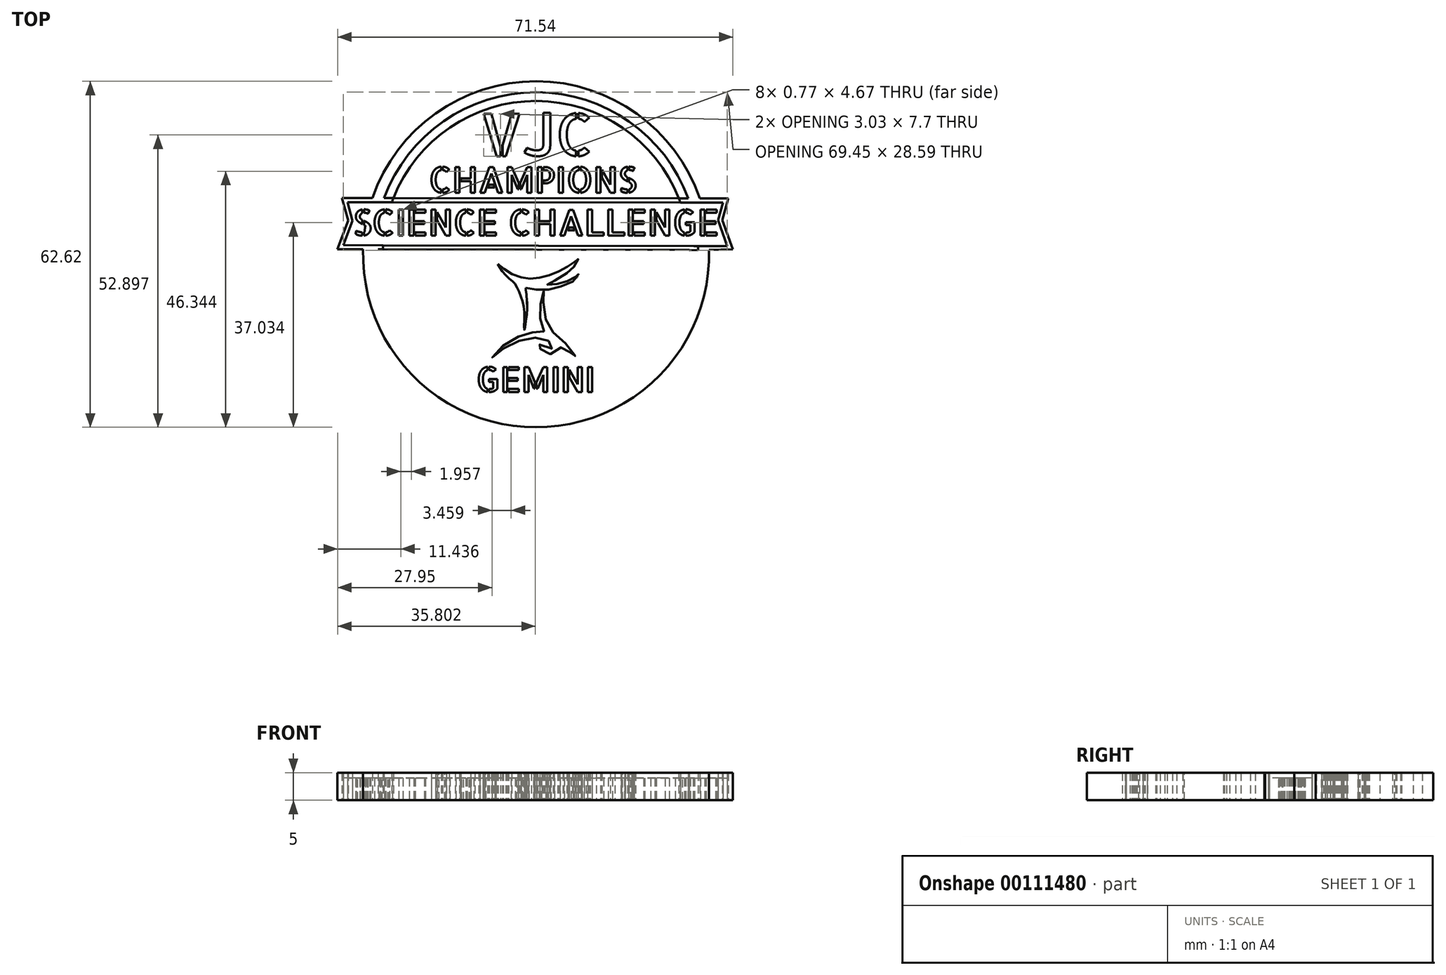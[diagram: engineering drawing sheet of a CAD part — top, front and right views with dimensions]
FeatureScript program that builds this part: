
annotation { "Feature Type Name" : "Feature", "Feature Type Description" : "" }
export const myFeature = defineFeature(function(context is Context, id is Id, definition is map)
    precondition{}
    {
        {
            var Q0;
            Q0=qCreatedBy(makeId("Top.planeOp"),FACE);
            var sketch = newSketch(context, id + "F0", { "sketchPlane" : qUnion([Q0])});
            skCircle(sketch, "E0", {"center": v(0.94, -3) * mm, "radius": 27.74 * mm});
            skPoint(sketch, "E0.first.point", {"position": v(1.58, 24.74) * mm});
            skPoint(sketch, "E0.second.point", {"position": v(0.52, -30.73) * mm});
            skPoint(sketch, "E0.third.point", {"position": v(-26.76, -1.33) * mm});
            skText(sketch, "E1", { "text": "CHAMPIONS", "fontName": "AllertaStencil-Regular.ttf"});
            skText(sketch, "E2", { "text": "GEMINI", "fontName": "AllertaStencil-Regular.ttf"});
            skLineSegment(sketch, "E3", {"start": v(-24.87, 7.2) * mm, "end": v(-34.2, 7.2) * mm});
            skLineSegment(sketch, "E4", {"start": v(-34.2, 7.2) * mm, "end": v(-33.08, 3.11) * mm});
            skLineSegment(sketch, "E5", {"start": v(-33.08, 3.11) * mm, "end": v(-35, -2.1) * mm});
            skLineSegment(sketch, "E6", {"start": v(-35, -2.1) * mm, "end": v(-26.8, -2.1) * mm});
            skLineSegment(sketch, "E7", {"start": v(26.78, 7.1) * mm, "end": v(35.71, 7.1) * mm});
            skLineSegment(sketch, "E8", {"start": v(35.71, 7.1) * mm, "end": v(34.66, 3.21) * mm});
            skLineSegment(sketch, "E9", {"start": v(34.66, 3.21) * mm, "end": v(36.55, -2.1) * mm});
            skLineSegment(sketch, "E10", {"start": v(36.55, -2.1) * mm, "end": v(28.67, -2.25) * mm});
            skFitSpline(sketch, "E11", {"points": [v(-6, -4.72) * mm, v(-5.23, -5.35) * mm, v(-3.9, -6.35) * mm, v(-2.48, -6.98) * mm, v(-0.85, -7.35) * mm, v(0.35, -7.37) * mm, v(2.08, -7.15) * mm, v(3.86, -6.6) * mm, v(5.5, -5.84) * mm, v(6.83, -5.05) * mm, v(7.95, -4.34) * mm, v(8.2, -4.17) * mm, v(8.54, -3.89) * mm, v(8.14, -4.78) * mm, v(7.2, -5.82) * mm, v(5.2, -7.28) * mm, v(2.9, -8.45) * mm, v(3.98, -8.47) * mm, v(5.87, -8.12) * mm, v(7.76, -7.26) * mm, v(8.43, -6.75) * mm, v(8.6, -6.46) * mm, v(8.47, -7.15) * mm, v(6.46, -8.4) * mm, v(3.8, -9.28) * mm, v(1.11, -9.42) * mm, v(-0.95, -9.06) * mm], "startDerivative": vector(22.31, -18.25) * mm, "endDerivative": vector(-43, 9.84) * mm});
            skFitSpline(sketch, "E12", {"points": [v(-6, -4.72) * mm, v(-5.19, -6.01) * mm, v(-3.81, -7.48) * mm, v(-3.02, -8.2) * mm, v(-2.26, -9.47) * mm, v(-1.53, -11.45) * mm, v(-1.17, -13.95) * mm, v(-1.2, -16.67) * mm, v(-0.95, -15.45) * mm, v(-0.68, -11.98) * mm, v(-0.91, -9.36) * mm, v(-0.95, -9.06) * mm], "startDerivative": vector(8.3, -15) * mm, "endDerivative": vector(-0.86, 6) * mm});
            skFitSpline(sketch, "E13", {"points": [v(2.34, -9.66) * mm, v(2.02, -10.62) * mm, v(1.67, -12.76) * mm, v(1.67, -14.3) * mm, v(2.06, -16.19) * mm, v(2.36, -16.95) * mm, v(1.82, -16.92) * mm, v(-0.01, -17.17) * mm, v(-1.66, -17.64) * mm, v(-3.97, -18.79) * mm, v(-6.02, -20.44) * mm, v(-6.96, -21.68) * mm, v(-5.91, -20.77) * mm, v(-3.67, -19.33) * mm, v(-1.3, -18.4) * mm, v(0.83, -18.07) * mm, v(2.42, -18.3) * mm, v(3.7, -19.03) * mm, v(4.04, -19.68) * mm, v(3.45, -20.21) * mm, v(1.98, -19.81) * mm, v(1.3, -18.87) * mm, v(1.45, -19.8) * mm, v(2.36, -20.56) * mm, v(3.3, -21.02) * mm, v(4.84, -20.7) * mm, v(5.53, -19.8) * mm, v(6.38, -20.28) * mm, v(7.16, -20.84) * mm, v(8.14, -21.87) * mm, v(7.64, -20.68) * mm, v(6.28, -19.14) * mm, v(4.5, -17.53) * mm, v(3.33, -16.29) * mm, v(2.56, -14.18) * mm, v(2.24, -11.68) * mm, v(2.33, -10.24) * mm, v(2.34, -9.66) * mm]});
            skLineSegment(sketch, "E14", {"start": v(-24.87, 7.2) * mm, "end": v(28.1, 7.1) * mm});
            skLineSegment(sketch, "E15", {"start": v(-27.68, -2.1) * mm, "end": v(29.48, -2.24) * mm});
            skText(sketch, "E16", { "text": "SCIENCE CHALLENGE", "fontName": "AllertaStencil-Regular.ttf"});
            skText(sketch, "E17", { "text": "VJC", "fontName": "AllertaStencil-Regular.ttf"});
            skCircle(sketch, "E18.0", {"center": v(0.94, -3) * mm, "radius": 29.33 * mm});
            skCircle(sketch, "E19.0", {"center": v(0.94, -3) * mm, "radius": 31.31 * mm});
            skLineSegment(sketch, "E20.0", {"start": v(-24.87, 6.45) * mm, "end": v(28.1, 6.35) * mm});
            skLineSegment(sketch, "E21.0", {"start": v(-24.87, 6.45) * mm, "end": v(-33.21, 6.45) * mm});
            skLineSegment(sketch, "E22", {"start": v(28.1, 6.35) * mm, "end": v(34.73, 6.35) * mm});
            skLineSegment(sketch, "E23.0", {"start": v(-27.68, -1.35) * mm, "end": v(29.48, -1.49) * mm});
            skLineSegment(sketch, "E24", {"start": v(-27.68, -1.35) * mm, "end": v(-33.91, -1.33) * mm});
            skLineSegment(sketch, "E25", {"start": v(29.48, -1.49) * mm, "end": v(35.54, -1.5) * mm});
            skLineSegment(sketch, "E26.0", {"start": v(34.73, 6.35) * mm, "end": v(33.88, 3.18) * mm});
            skLineSegment(sketch, "E27.0", {"start": v(33.88, 3.18) * mm, "end": v(35.54, -1.5) * mm});
            skLineSegment(sketch, "E28.0", {"start": v(-32.3, 3.08) * mm, "end": v(-33.91, -1.33) * mm});
            skLineSegment(sketch, "E29.trimOffspring", {"start": v(-33.21, 6.45) * mm, "end": v(-32.3, 3.08) * mm});
            const initialGuessF0  = {"E1": [-0.01849, 0.00816, 1, 0, 0.00464], "E2": [-0.00992, -0.0279, 1, 0, 0.0045], "E16": [-0.03222, 0.0004, 1, 0, 0.00467], "E17": [-0.00918, 0.01479, 1, 0, 0.00766]};
            skSetInitialGuess(sketch, initialGuessF0);
            skSolve(sketch);
        }
        {
            var Q0;
            Q0=makeQuery(id+"F0.imprint","IMPRINT",FACE,{"disambiguationData":[TD([[makeQuery(id+"F0.imprint","IMPRINT",EDGE,{"derivedFrom":sQuery(id+"F0.wireOp",EDGE,"E1.sketch_text.stroke-0")}),1.0]])]});
            var Q1;
            {var subQ0=sQuery(id+"F0.wireOp",EDGE,"E19.0");var subQ1=sQuery(id+"F0.wireOp",EDGE,"E3");var subQ2=makeQuery(id+"F0.imprint","INTERSECT",VERTEX,{"derivedFrom":[subQ1,subQ0]});Q1=makeQuery(id+"F0.imprint","IMPRINT",FACE,{"disambiguationData":[TD([[makeQuery(id+"F0.imprint","IMPRINT",EDGE,{"disambiguationData":[TD([[subQ2,1.0]])],"derivedFrom":subQ1}),-1.0]])]});}
            var Q2;
            Q2=makeQuery(id+"F0.imprint","IMPRINT",FACE,{"disambiguationData":[TD([[makeQuery(id+"F0.imprint","IMPRINT",EDGE,{"derivedFrom":sQuery(id+"F0.wireOp",EDGE,"E2.sketch_text.stroke-0")}),1.0]])]});
            var Q3;
            {var subQ0=sQuery(id+"F0.wireOp",EDGE,"E19.0");var subQ1=sQuery(id+"F0.wireOp",EDGE,"E6");var subQ2=makeQuery(id+"F0.imprint","INTERSECT",VERTEX,{"derivedFrom":[subQ1,subQ0]});Q3=makeQuery(id+"F0.imprint","IMPRINT",FACE,{"disambiguationData":[TD([[makeQuery(id+"F0.imprint","IMPRINT",EDGE,{"disambiguationData":[TD([[subQ2,-1.0]])],"derivedFrom":subQ1}),-1.0]])]});}
            var Q4;
            {var subQ7=sQuery(id+"F0.wireOp",EDGE,"E4");Q4=makeQuery(id+"F0.imprint","IMPRINT",FACE,{"disambiguationData":[TD([[makeQuery(id+"F0.imprint","IMPRINT",EDGE,{"derivedFrom":subQ7}),1.0]])]});}
            var Q5;
            {var subQ3=sQuery(id+"F0.wireOp",EDGE,"E21.0");var subQ10=makeQuery(id+"F0.imprint","IMPRINT",VERTEX,{"derivedFrom":subQ3});Q5=makeQuery(id+"F0.imprint","IMPRINT",FACE,{"disambiguationData":[TD([[makeQuery(id+"F0.imprint","IMPRINT",EDGE,{"disambiguationData":[TD([[subQ10,1.0]])],"derivedFrom":subQ3}),-1.0]])]});}
            var Q6;
            {var subQ0=sQuery(id+"F0.wireOp",EDGE,"E3");var subQ5=sQuery(id+"F0.wireOp",EDGE,"E18.0");var subQ6=makeQuery(id+"F0.imprint","INTERSECT",VERTEX,{"derivedFrom":[subQ0,subQ5]});Q6=makeQuery(id+"F0.imprint","IMPRINT",FACE,{"disambiguationData":[TD([[makeQuery(id+"F0.imprint","IMPRINT",EDGE,{"disambiguationData":[TD([[subQ6,-1.0]])],"derivedFrom":subQ5}),1.0]])]});}
            var Q7;
            {var subQ1=sQuery(id+"F0.wireOp",EDGE,"E7");var subQ6=sQuery(id+"F0.wireOp",EDGE,"E0");var subQ7=makeQuery(id+"F0.imprint","INTERSECT",VERTEX,{"derivedFrom":[subQ6,subQ1]});Q7=makeQuery(id+"F0.imprint","IMPRINT",FACE,{"disambiguationData":[TD([[makeQuery(id+"F0.imprint","IMPRINT",EDGE,{"disambiguationData":[TD([[subQ7,1.0]])],"derivedFrom":subQ6}),-1.0]])]});}
            var Q8;
            {var subQ0=sQuery(id+"F0.wireOp",EDGE,"E19.0");var subQ1=sQuery(id+"F0.wireOp",EDGE,"E7");var subQ2=makeQuery(id+"F0.imprint","INTERSECT",VERTEX,{"derivedFrom":[subQ1,subQ0]});Q8=makeQuery(id+"F0.imprint","IMPRINT",FACE,{"disambiguationData":[TD([[makeQuery(id+"F0.imprint","IMPRINT",EDGE,{"disambiguationData":[TD([[subQ2,1.0]])],"derivedFrom":subQ1}),-1.0]])]});}
            var Q9;
            {var subQ11=sQuery(id+"F0.wireOp",EDGE,"E8");Q9=makeQuery(id+"F0.imprint","IMPRINT",FACE,{"disambiguationData":[TD([[makeQuery(id+"F0.imprint","IMPRINT",EDGE,{"derivedFrom":subQ11}),-1.0]])]});}
            var Q10;
            {var subQ0=sQuery(id+"F0.wireOp",EDGE,"E15");var subQ1=sQuery(id+"F0.wireOp",EDGE,"E0");var subQ2=makeQuery(id+"F0.imprint","INTERSECT",VERTEX,{"disambiguationData":[OD(0.0)],"derivedFrom":[subQ1,subQ0]});Q10=makeQuery(id+"F0.imprint","IMPRINT",FACE,{"disambiguationData":[TD([[makeQuery(id+"F0.imprint","IMPRINT",EDGE,{"disambiguationData":[TD([[subQ2,-1.0]])],"derivedFrom":subQ1}),1.0]])]});}
            var Q11;
            {var subQ0=sQuery(id+"F0.wireOp",EDGE,"E15");var subQ3=sQuery(id+"F0.wireOp",EDGE,"E0");var subQ4=makeQuery(id+"F0.imprint","INTERSECT",VERTEX,{"disambiguationData":[OD(0.0)],"derivedFrom":[subQ3,subQ0]});Q11=makeQuery(id+"F0.imprint","IMPRINT",FACE,{"disambiguationData":[TD([[makeQuery(id+"F0.imprint","IMPRINT",EDGE,{"disambiguationData":[TD([[subQ4,-1.0]])],"derivedFrom":subQ3}),-1.0]])]});}
            var Q12;
            {var subQ0=sQuery(id+"F0.wireOp",EDGE,"E19.0");var subQ1=sQuery(id+"F0.wireOp",EDGE,"E10");var subQ2=makeQuery(id+"F0.imprint","INTERSECT",VERTEX,{"derivedFrom":[subQ1,subQ0]});Q12=makeQuery(id+"F0.imprint","IMPRINT",FACE,{"disambiguationData":[TD([[makeQuery(id+"F0.imprint","IMPRINT",EDGE,{"disambiguationData":[TD([[subQ2,-1.0]])],"derivedFrom":subQ1}),-1.0]])]});}
            var Q13;
            {var subQ0=sQuery(id+"F0.wireOp",EDGE,"E19.0");var subQ1=sQuery(id+"F0.wireOp",EDGE,"E3");var subQ2=makeQuery(id+"F0.imprint","INTERSECT",VERTEX,{"derivedFrom":[subQ1,subQ0]});Q13=makeQuery(id+"F0.imprint","IMPRINT",FACE,{"disambiguationData":[TD([[makeQuery(id+"F0.imprint","IMPRINT",EDGE,{"disambiguationData":[TD([[subQ2,1.0]])],"derivedFrom":subQ1}),1.0]])]});}
            var Q14;
            {var subQ0=sQuery(id+"F0.wireOp",EDGE,"E19.0");var subQ1=sQuery(id+"F0.wireOp",EDGE,"E6");var subQ2=makeQuery(id+"F0.imprint","INTERSECT",VERTEX,{"derivedFrom":[subQ1,subQ0]});Q14=makeQuery(id+"F0.imprint","IMPRINT",FACE,{"disambiguationData":[TD([[makeQuery(id+"F0.imprint","IMPRINT",EDGE,{"disambiguationData":[TD([[subQ2,-1.0]])],"derivedFrom":subQ1}),1.0]])]});}
            var Q15;
            {var subQ0=sQuery(id+"F0.wireOp",EDGE,"E6");var subQ1=sQuery(id+"F0.wireOp",EDGE,"E0");var subQ2=makeQuery(id+"F0.imprint","INTERSECT",VERTEX,{"derivedFrom":[subQ1,subQ0]});Q15=makeQuery(id+"F0.imprint","IMPRINT",FACE,{"disambiguationData":[TD([[makeQuery(id+"F0.imprint","IMPRINT",EDGE,{"disambiguationData":[TD([[subQ2,1.0]])],"derivedFrom":subQ1}),-1.0]])]});}
            extrude(context, id + "F1", {"entities" : qUnion([Q0, Q1, Q2, Q3, Q4, Q5, Q6, Q7, Q8, Q9, Q10, Q11, Q12, Q13, Q14, Q15]), "depth" : 5 * mm});
        }
        {
            var Q0;
            {var subQ20=sQuery(id+"F0.wireOp",EDGE,"E16.sketch_text.stroke-1");Q0=makeQuery(id+"F0.imprint","IMPRINT",FACE,{"disambiguationData":[TD([[makeQuery(id+"F0.imprint","IMPRINT",EDGE,{"derivedFrom":subQ20}),1.0]])]});}
            var Q1;
            {var subQ18=sQuery(id+"F0.wireOp",EDGE,"E16.sketch_text.stroke-7");Q1=makeQuery(id+"F0.imprint","IMPRINT",FACE,{"disambiguationData":[TD([[makeQuery(id+"F0.imprint","IMPRINT",EDGE,{"derivedFrom":subQ18}),1.0]])]});}
            var Q2;
            {var subQ11=sQuery(id+"F0.wireOp",EDGE,"E16.sketch_text.stroke-54");Q2=makeQuery(id+"F0.imprint","IMPRINT",FACE,{"disambiguationData":[TD([[makeQuery(id+"F0.imprint","IMPRINT",EDGE,{"derivedFrom":subQ11}),1.0]])]});}
            var Q3;
            {var subQ25=sQuery(id+"F0.wireOp",EDGE,"E16.sketch_text.stroke-246");Q3=makeQuery(id+"F0.imprint","IMPRINT",FACE,{"disambiguationData":[TD([[makeQuery(id+"F0.imprint","IMPRINT",EDGE,{"derivedFrom":subQ25}),1.0]])]});}
            var Q4;
            {var subQ11=sQuery(id+"F0.wireOp",EDGE,"E16.sketch_text.stroke-289");Q4=makeQuery(id+"F0.imprint","IMPRINT",FACE,{"disambiguationData":[TD([[makeQuery(id+"F0.imprint","IMPRINT",EDGE,{"derivedFrom":subQ11}),1.0]])]});}
            var Q5;
            {var subQ12=sQuery(id+"F0.wireOp",EDGE,"E16.sketch_text.stroke-293");Q5=makeQuery(id+"F0.imprint","IMPRINT",FACE,{"disambiguationData":[TD([[makeQuery(id+"F0.imprint","IMPRINT",EDGE,{"derivedFrom":subQ12}),1.0]])]});}
            var Q6;
            {var subQ0=sQuery(id+"F0.wireOp",EDGE,"E16.sketch_text.stroke-281");Q6=makeQuery(id+"F0.imprint","IMPRINT",FACE,{"disambiguationData":[TD([[makeQuery(id+"F0.imprint","IMPRINT",EDGE,{"derivedFrom":subQ0}),1.0]])]});}
            var Q7;
            {var subQ14=sQuery(id+"F0.wireOp",EDGE,"E16.sketch_text.stroke-51");Q7=makeQuery(id+"F0.imprint","IMPRINT",FACE,{"disambiguationData":[TD([[makeQuery(id+"F0.imprint","IMPRINT",EDGE,{"derivedFrom":subQ14}),1.0]])]});}
            var Q8;
            {var subQ1=sQuery(id+"F0.wireOp",EDGE,"E16.sketch_text.stroke-76");Q8=makeQuery(id+"F0.imprint","IMPRINT",FACE,{"disambiguationData":[TD([[makeQuery(id+"F0.imprint","IMPRINT",EDGE,{"derivedFrom":subQ1}),1.0]])]});}
            extrude(context, id + "F2", {"entities" : qUnion([Q0, Q1, Q2, Q3, Q4, Q5, Q6, Q7, Q8]), "depth" : 4 * mm});
        }
    });
